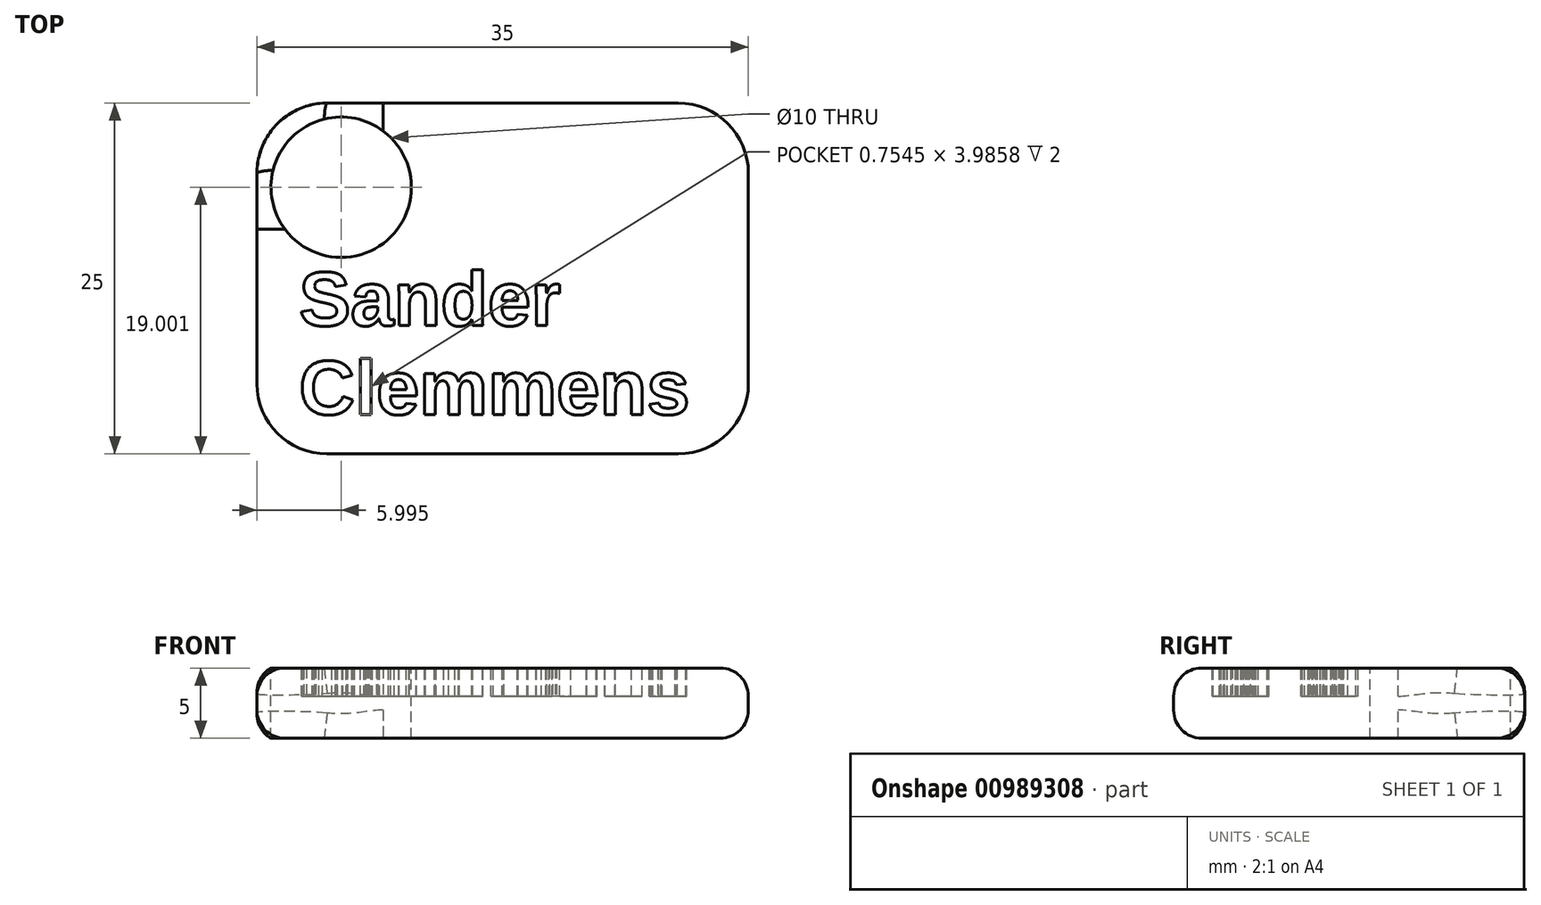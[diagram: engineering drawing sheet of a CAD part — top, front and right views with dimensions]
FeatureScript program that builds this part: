
annotation { "Feature Type Name" : "Feature", "Feature Type Description" : "" }
export const myFeature = defineFeature(function(context is Context, id is Id, definition is map)
    precondition{}
    {
        {
            var Q0;
            Q0=qCreatedBy(makeId("Top.planeOp"),FACE);
            var sketch = newSketch(context, id + "F0", { "sketchPlane" : qUnion([Q0])});
            skLineSegment(sketch, "E0.bottom", {"start": v(-10.23, -4.08) * mm, "end": v(14.77, -4.08) * mm});
            skLineSegment(sketch, "E0.top", {"start": v(-10.23, -29.08) * mm, "end": v(14.77, -29.08) * mm});
            skLineSegment(sketch, "E0.left", {"start": v(-15.23, -9.08) * mm, "end": v(-15.23, -24.08) * mm});
            skLineSegment(sketch, "E0.right", {"start": v(19.77, -9.08) * mm, "end": v(19.77, -24.08) * mm});
            skPoint(sketch, "E1.visualSharp", {"position": v(-15.23, -29.08) * mm});
            skArc(sketch, "E1.filletArc", {"start": v(-15.23, -24.08) * mm, "mid": v(-13.77, -27.61) * mm, "end": v(-10.23, -29.08) * mm});
            skPoint(sketch, "E2.visualSharp", {"position": v(-15.23, -4.08) * mm});
            skArc(sketch, "E2.filletArc", {"start": v(-10.23, -4.08) * mm, "mid": v(-13.77, -5.54) * mm, "end": v(-15.23, -9.08) * mm});
            skPoint(sketch, "E3.visualSharp", {"position": v(19.77, -4.08) * mm});
            skArc(sketch, "E3.filletArc", {"start": v(19.77, -9.08) * mm, "mid": v(18.3, -5.54) * mm, "end": v(14.77, -4.08) * mm});
            skPoint(sketch, "E4.visualSharp", {"position": v(19.77, -29.08) * mm});
            skArc(sketch, "E4.filletArc", {"start": v(14.77, -29.08) * mm, "mid": v(18.3, -27.61) * mm, "end": v(19.77, -24.08) * mm});
            skSolve(sketch);
        }
        {
            var Q0;
            Q0=makeQuery(id+"F0.imprint","IMPRINT",FACE,{"disambiguationData":[TD([[makeQuery(id+"F0.imprint","IMPRINT",EDGE,{"derivedFrom":sQuery(id+"F0.wireOp",EDGE,"E0.bottom")}),-1.0]])]});
            extrude(context, id + "F1", {"entities" : qUnion([Q0]), "depth" : 5 * mm, "offsetDistance" : 25 * mm});
        }
        {
            var Q0;
            Q0=makeQuery(id+"F1.opExtrude","CAP_FACE",FACE,{"disambiguationData":[OSD([sQuery(id+"F0.wireOp",EDGE,"E0.bottom"),sQuery(id+"F0.wireOp",EDGE,"E0.top"),sQuery(id+"F0.wireOp",EDGE,"E0.left"),sQuery(id+"F0.wireOp",EDGE,"E0.right"),sQuery(id+"F0.wireOp",EDGE,"E1.filletArc"),sQuery(id+"F0.wireOp",EDGE,"E2.filletArc"),sQuery(id+"F0.wireOp",EDGE,"E3.filletArc"),sQuery(id+"F0.wireOp",EDGE,"E4.filletArc")])],"isStart":false});
            var sketch = newSketch(context, id + "F2", { "sketchPlane" : qUnion([Q0])});
            skCircle(sketch, "E5", {"center": v(-9.23, -10.08) * mm, "radius": 5 * mm});
            skSolve(sketch);
        }
        {
            var Q0;
            Q0=makeQuery(id+"F2.imprint","IMPRINT",FACE,{"disambiguationData":[TD([[makeQuery(id+"F2.imprint","IMPRINT",EDGE,{"derivedFrom":sQuery(id+"F2.wireOp",EDGE,"E5")}),1.0]])]});
            extrude(context, id + "F3", {"entities" : qUnion([Q0]), "operationType" : NewBodyOperationType.REMOVE, "oppositeDirection" : true, "depth" : 25 * mm, "offsetDistance" : 25 * mm});
        }
        {
            var Q0;
            Q0=makeQuery(id+"F1.opExtrude","CAP_EDGE",EDGE,{"disambiguationData":[OSD([sQuery(id+"F0.wireOp",EDGE,"E0.bottom")])],"isStart":false});
            var Q1;
            Q1=makeQuery(id+"F1.opExtrude","CAP_EDGE",EDGE,{"disambiguationData":[OSD([sQuery(id+"F0.wireOp",EDGE,"E0.bottom")])],"isStart":true});
            fillet(context, id + "F4", {"entities" : qUnion([Q0, Q1]), "radius" : 2 * mm, "tangentPropagation" : true, "allowEdgeOverflow" : false});
        }
        {
            var Q0;
            Q0=makeQuery(id+"F1.opExtrude","CAP_FACE",FACE,{"disambiguationData":[OSD([sQuery(id+"F0.wireOp",EDGE,"E0.bottom"),sQuery(id+"F0.wireOp",EDGE,"E0.top"),sQuery(id+"F0.wireOp",EDGE,"E0.left"),sQuery(id+"F0.wireOp",EDGE,"E0.right"),sQuery(id+"F0.wireOp",EDGE,"E1.filletArc"),sQuery(id+"F0.wireOp",EDGE,"E2.filletArc"),sQuery(id+"F0.wireOp",EDGE,"E3.filletArc"),sQuery(id+"F0.wireOp",EDGE,"E4.filletArc")])],"isStart":false});
            var sketch = newSketch(context, id + "F5", { "sketchPlane" : qUnion([Q0])});
            skText(sketch, "E6", { "text": "Sander \nClemmens", "fontName": "Arimo-Bold.ttf"});
            const initialGuessF5  = {"E6": [-0.01223, -0.01994, 1, 0, 0.00396]};
            skSetInitialGuess(sketch, initialGuessF5);
            skSolve(sketch);
        }
        {
            var Q0;
            Q0 = qSketchRegion(id + "F5", true);
            extrude(context, id + "F6", {"entities" : qUnion([Q0]), "operationType" : NewBodyOperationType.REMOVE, "oppositeDirection" : true, "depth" : 2 * mm, "offsetDistance" : 25 * mm});
        }
    });
